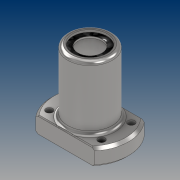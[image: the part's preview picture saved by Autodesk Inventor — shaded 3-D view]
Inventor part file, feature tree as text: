
AUTODESK INVENTOR PART (.ipt)
format: ipt  version: 2021 (Build 250183000, 183)  size: 248,320 bytes
history: native  units: mm
features: sketch x4, extrude x4, fillet x2, plane x2, chamfer x2, projected_geometry x2, hole x1
ambient origin geometry x8: Origin, YZ Plane, XZ Plane, XY Plane, X Axis, Y Axis, Z Axis, Center Point
bodies: Solid1 (feature_tree)
feature tree (17):
  sketch  "Sketch1"  dims[d0=29.0mm d1=45.0mm]
  extrude  "Extrusion1"  Depth=45.0mm
  extrude  "Extrusion2"  Depth=10.0mm
  fillet  "Fillet1"  Radius=10.0mm
  plane  "Work Plane1"
  extrude  "Extrusion3"  Depth=2.0mm
  plane  "Work Plane2"
  extrude  "Extrusion4"  Depth=4.0mm
  chamfer  "Chamfer1"  Distance=1.25mm
  chamfer  "Chamfer2"  [1 undecoded]
  fillet  "Fillet2"  Radius=14.0mm
  hole  "Hole1"  [1 undecoded]
  sketch  "Sketch2"  dims[d2=20.0mm d3=26.0mm d4=10.0mm d5=0.0mm]
  sketch  "Sketch3"  dims[d6=37.0mm d7=0.0mm d8=2.0mm]
  projected_geometry  "Projected Loop1"
  sketch  "Sketch4"  dims[d9=-3.0mm d10=14.0mm d11=1.25mm d12=0.0mm d13=-1.25mm d14=14.0mm d15=1.0mm d16=0.0mm d17=0.5mm d18=2.0mm d19=45.0deg d20=1.5mm d21=2.0mm d22=45.0deg d23=2.0mm d24=17.4mm d25=30.2mm d26=4.0mm d27=6.0mm d28=8.0mm d29=3.0mm d30=90.0deg d31=12.5mm d32=20.594885mm]
  projected_geometry  "Projected Loop2"
note: 2 required parameter values undecoded (feature->parameter linkage not recoverable at this tier; creation-order binding heuristic only, values carry confidence <= 0.55)
